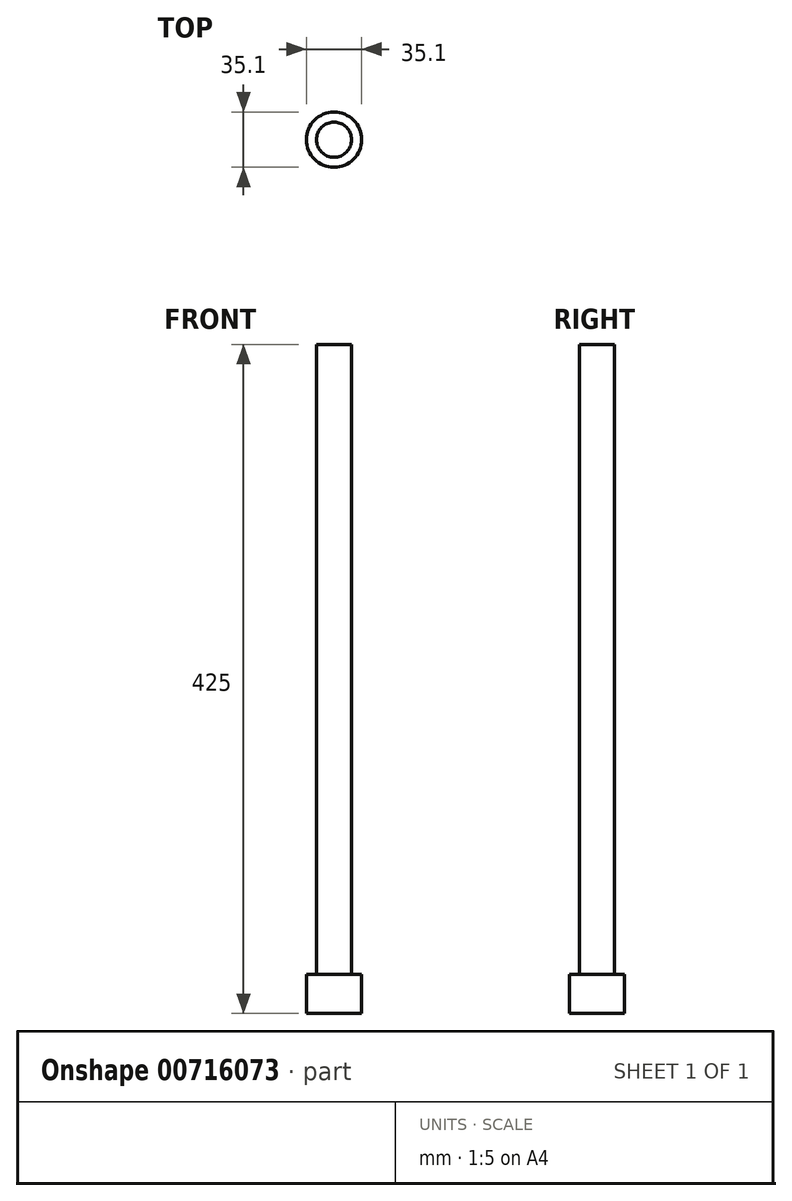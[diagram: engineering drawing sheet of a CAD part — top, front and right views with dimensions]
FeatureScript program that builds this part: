
annotation { "Feature Type Name" : "Feature", "Feature Type Description" : "" }
export const myFeature = defineFeature(function(context is Context, id is Id, definition is map)
    precondition{}
    {
        {
            var Q0;
            Q0=qCreatedBy(makeId("Top.planeOp"),FACE);
            var sketch = newSketch(context, id + "F0", { "sketchPlane" : qUnion([Q0])});
            skPoint(sketch, "E0.middle", {"position": v(0, 0) * mm});
            skCircle(sketch, "E1", {"center": v(0, 0) * mm, "radius": 11.17 * mm});
            skCircle(sketch, "E2", {"center": v(0, 0) * mm, "radius": 17.55 * mm});
            skSolve(sketch);
        }
        {
            var Q0;
            Q0=makeQuery(id+"F0.imprint","IMPRINT",FACE,{"disambiguationData":[TD([[makeQuery(id+"F0.imprint","IMPRINT",EDGE,{"derivedFrom":sQuery(id+"F0.wireOp",EDGE,"E1")}),1.0]])]});
            extrude(context, id + "F1", {"entities" : qUnion([Q0]), "depth" : 400 * mm, "offsetDistance" : 25 * mm});
        }
        {
            var Q0;
            Q0 = qSketchRegion(id + "F0", true);
            var Q1;
            Q1=makeQuery(id+"F0.imprint","IMPRINT",FACE,{"disambiguationData":[TD([[makeQuery(id+"F0.imprint","IMPRINT",EDGE,{"derivedFrom":sQuery(id+"F0.wireOp",EDGE,"E1")}),1.0]])]});
            var Q2;
            Q2=sQuery(id+"F0.wireOp",EDGE,"E2");
            extrude(context, id + "F2", {"entities" : qUnion([Q0, Q1]), "operationType" : NewBodyOperationType.ADD, "surfaceEntities" : qUnion([Q2]), "oppositeDirection" : true, "depth" : 25 * mm, "offsetDistance" : 25 * mm});
        }
    });
